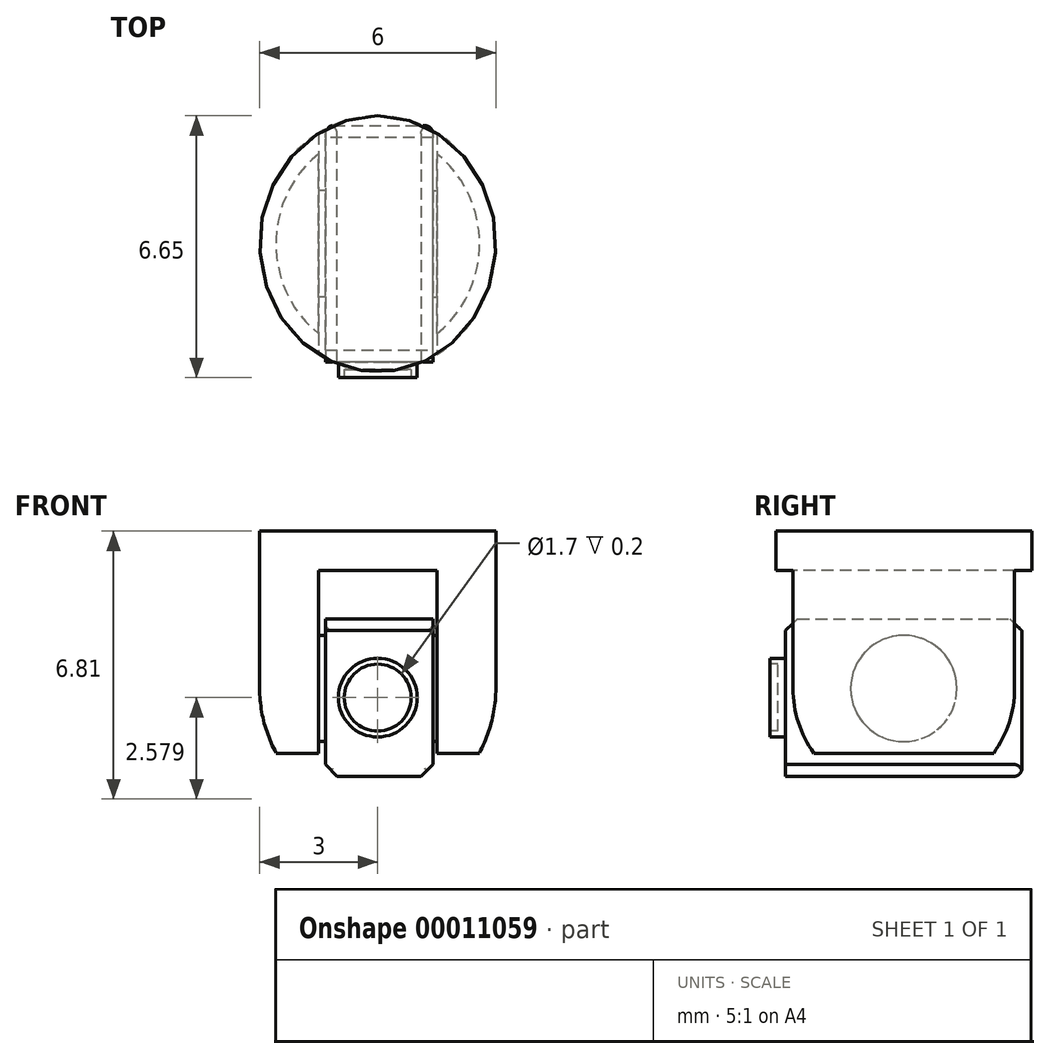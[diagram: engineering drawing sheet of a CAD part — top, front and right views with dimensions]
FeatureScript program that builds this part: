
annotation { "Feature Type Name" : "Feature", "Feature Type Description" : "" }
export const myFeature = defineFeature(function(context is Context, id is Id, definition is map)
    precondition{}
    {
        {
            var Q0;
            Q0=qCreatedBy(makeId("Top.planeOp"),FACE);
            var sketch = newSketch(context, id + "F0", { "sketchPlane" : qUnion([Q0])});
            skEllipse(sketch, "E0", {"center": v(0, 0) * mm, "majorRadius": 3 * mm, "minorRadius": 3.25 * mm, "majorAxis": v(1, 0)});
            skSolve(sketch);
        }
        {
            var Q0;
            Q0 = qSketchRegion(id + "F0", true);
            extrude(context, id + "F1", {"entities" : qUnion([Q0]), "oppositeDirection" : true, "depth" : 4 * mm});
        }
        {
            var Q0;
            Q0=makeQuery(id+"F1.opExtrude","CAP_FACE",FACE,{"disambiguationData":[OSD([sQuery(id+"F0.wireOp",EDGE,"E0")])],"isStart":false});
            var sketch = newSketch(context, id + "F2", { "sketchPlane" : qUnion([Q0])});
            skEllipse(sketch, "E1", {"center": v(0, 0) * mm, "majorRadius": 3.25 * mm, "minorRadius": 3 * mm, "majorAxis": v(0, -1)});
            skLineSegment(sketch, "E2", {"start": v(-3, 0) * mm, "end": v(3, 0) * mm});
            skSolve(sketch);
        }
        {
            var Q0;
            {var subQ0=sQuery(id+"F2.wireOp",EDGE,"E2");Q0=makeQuery(id+"F2.imprint","IMPRINT",FACE,{"disambiguationData":[TD([[makeQuery(id+"F2.imprint","IMPRINT",EDGE,{"derivedFrom":subQ0}),-1.0]])]});}
            var Q1;
            Q1=sQuery(id+"F2.wireOp",EDGE,"E2");
            revolve(context, id + "F3", {"operationType" : NewBodyOperationType.ADD, "entities" : qUnion([Q0]), "axis" : qUnion([Q1]), "revolveType" : RevolveType.FULL});
        }
        {
            var Q0;
            Q0=qCreatedBy(makeId("Top.planeOp"),FACE);
            var sketch = newSketch(context, id + "F4", { "sketchPlane" : qUnion([Q0])});
            skLineSegment(sketch, "E3.rect.bottom", {"start": v(1.5, 4) * mm, "end": v(-1.5, 4) * mm});
            skLineSegment(sketch, "E3.rect.top", {"start": v(1.5, -4) * mm, "end": v(-1.5, -4) * mm});
            skLineSegment(sketch, "E3.rect.left", {"start": v(1.5, 4) * mm, "end": v(1.5, -4) * mm});
            skLineSegment(sketch, "E3.rect.right", {"start": v(-1.5, 4) * mm, "end": v(-1.5, -4) * mm});
            skPoint(sketch, "E3.rect.middle", {"position": v(0, 0) * mm});
            skSolve(sketch);
        }
        {
            var Q0;
            Q0=makeQuery(id+"F4.imprint","IMPRINT",FACE,{"disambiguationData":[TD([[makeQuery(id+"F4.imprint","IMPRINT",EDGE,{"derivedFrom":sQuery(id+"F4.wireOp",EDGE,"E3.rect.bottom")}),1.0]])]});
            extrude(context, id + "F5", {"entities" : qUnion([Q0]), "operationType" : NewBodyOperationType.REMOVE, "oppositeDirection" : true, "depth" : 25 * mm, "hasSecondDirection" : true, "secondDirectionOppositeDirection" : true, "secondDirectionDepth" : 1 * mm});
        }
        {
            var Q0;
            Q0=qCreatedBy(makeId("Front.planeOp"),FACE);
            var sketch = newSketch(context, id + "F6", { "sketchPlane" : qUnion([Q0])});
            skLineSegment(sketch, "E4.rect.bottom", {"start": v(3.25, -7.37) * mm, "end": v(-3.25, -7.37) * mm});
            skLineSegment(sketch, "E4.rect.top", {"start": v(3.25, -5.64) * mm, "end": v(-3.25, -5.64) * mm});
            skLineSegment(sketch, "E4.rect.left", {"start": v(3.25, -7.37) * mm, "end": v(3.25, -5.64) * mm});
            skLineSegment(sketch, "E4.rect.right", {"start": v(-3.25, -7.37) * mm, "end": v(-3.25, -5.64) * mm});
            skPoint(sketch, "E4.rect.middle", {"position": v(0, -6.5) * mm});
            skSolve(sketch);
        }
        {
            var Q0;
            Q0 = qSketchRegion(id + "F6", true);
            extrude(context, id + "F7", {"entities" : qUnion([Q0]), "operationType" : NewBodyOperationType.REMOVE, "endBound" : BoundingType.SYMMETRIC, "oppositeDirection" : true, "depth" : 25 * mm});
        }
        {
            var Q0;
            Q0=makeQuery(id+"F5.boolean.opBoolean","COPY",FACE,{"derivedFrom":makeQuery(id+"F5.opExtrude","SWEPT_FACE",FACE,{"disambiguationData":[OSD([sQuery(id+"F4.wireOp",EDGE,"E3.rect.left")])]})});
            var sketch = newSketch(context, id + "F8", { "sketchPlane" : qUnion([Q0])});
            skCircle(sketch, "E5", {"center": v(0, -4) * mm, "radius": 1.35 * mm});
            skSolve(sketch);
        }
        {
            var Q0;
            Q0 = qSketchRegion(id + "F8", true);
            extrude(context, id + "F9", {"entities" : qUnion([Q0]), "operationType" : NewBodyOperationType.ADD, "depth" : 0.1 * mm});
        }
        {
            var Q0;
            Q0=makeQuery(id+"F5.boolean.opBoolean","COPY",FACE,{"derivedFrom":makeQuery(id+"F5.opExtrude","SWEPT_FACE",FACE,{"disambiguationData":[OSD([sQuery(id+"F4.wireOp",EDGE,"E3.rect.right")])]})});
            var sketch = newSketch(context, id + "F10", { "sketchPlane" : qUnion([Q0])});
            skCircle(sketch, "E6", {"center": v(0, -4) * mm, "radius": 1.35 * mm});
            skSolve(sketch);
        }
        {
            var Q0;
            Q0 = qSketchRegion(id + "F10", true);
            extrude(context, id + "F11", {"entities" : qUnion([Q0]), "operationType" : NewBodyOperationType.ADD, "depth" : 0.17 * mm});
        }
        {
            var Q0;
            Q0=qCreatedBy(makeId("Front.planeOp"),FACE);
            var sketch = newSketch(context, id + "F12", { "sketchPlane" : qUnion([Q0])});
            skPoint(sketch, "E7", {"position": v(-1.5, -4) * mm});
            skPoint(sketch, "E8", {"position": v(1.5, -4) * mm});
            skLineSegment(sketch, "E9", {"start": v(-1.33, 0.8) * mm, "end": v(-1.33, -8.05) * mm, "construction": true});
            skLineSegment(sketch, "E10", {"start": v(1.4, 0.83) * mm, "end": v(1.4, -8.97) * mm, "construction": true});
            skLineSegment(sketch, "E11.bottom", {"start": v(-1.33, -2.23) * mm, "end": v(1.4, -2.23) * mm});
            skLineSegment(sketch, "E11.top", {"start": v(-1.33, -6.23) * mm, "end": v(1.4, -6.23) * mm});
            skLineSegment(sketch, "E11.left", {"start": v(-1.33, -2.23) * mm, "end": v(-1.33, -6.23) * mm});
            skLineSegment(sketch, "E11.right", {"start": v(1.4, -2.23) * mm, "end": v(1.4, -6.23) * mm});
            skSolve(sketch);
        }
        {
            var Q0;
            Q0 = qSketchRegion(id + "F12", true);
            extrude(context, id + "F13", {"entities" : qUnion([Q0]), "depth" : 3 * mm});
        }
        {
            var Q0;
            Q0=makeQuery(id+"F13.opExtrude","CAP_FACE",FACE,{"disambiguationData":[OSD([sQuery(id+"F12.wireOp",EDGE,"E11.bottom"),sQuery(id+"F12.wireOp",EDGE,"E11.top"),sQuery(id+"F12.wireOp",EDGE,"E11.left"),sQuery(id+"F12.wireOp",EDGE,"E11.right")])],"isStart":true});
            extrude(context, id + "F14", {"entities" : qUnion([Q0]), "operationType" : NewBodyOperationType.ADD, "depth" : 3 * mm});
        }
        {
            var Q0;
            Q0=makeQuery(id+"F13.opExtrude","CAP_FACE",FACE,{"disambiguationData":[OSD([sQuery(id+"F12.wireOp",EDGE,"E11.bottom"),sQuery(id+"F12.wireOp",EDGE,"E11.top"),sQuery(id+"F12.wireOp",EDGE,"E11.left"),sQuery(id+"F12.wireOp",EDGE,"E11.right")])],"isStart":false});
            var sketch = newSketch(context, id + "F15", { "sketchPlane" : qUnion([Q0])});
            skSolve(sketch);
        }
        {
            var Q0;
            Q0=makeQuery(id+"F15.imprint","IMPRINT",FACE,{"disambiguationData":[TD([[makeQuery(id+"F15.imprint","IMPRINT",EDGE,{"derivedFrom":makeQuery(id+"F13.opExtrude","CAP_EDGE",EDGE,{"disambiguationData":[OSD([sQuery(id+"F12.wireOp",EDGE,"E11.bottom")])],"isStart":false})}),-1.0]])]});
            var sketch = newSketch(context, id + "F16", { "sketchPlane" : qUnion([Q0])});
            skCircle(sketch, "E12", {"center": v(0, -4.23) * mm, "radius": 1 * mm});
            skSolve(sketch);
        }
        {
            var Q0;
            Q0 = qSketchRegion(id + "F16", true);
            extrude(context, id + "F17", {"entities" : qUnion([Q0]), "operationType" : NewBodyOperationType.ADD, "depth" : 0.4 * mm});
        }
        {
            var Q0;
            Q0=makeQuery(id+"F17.opExtrude","CAP_FACE",FACE,{"disambiguationData":[OSD([sQuery(id+"F16.wireOp",EDGE,"E12")])],"isStart":false});
            var sketch = newSketch(context, id + "F18", { "sketchPlane" : qUnion([Q0])});
            skCircle(sketch, "E13", {"center": v(0, -4.23) * mm, "radius": 0.85 * mm});
            skSolve(sketch);
        }
        {
            var Q0;
            Q0 = qSketchRegion(id + "F18", true);
            extrude(context, id + "F19", {"entities" : qUnion([Q0]), "operationType" : NewBodyOperationType.REMOVE, "oppositeDirection" : true, "depth" : 0.2 * mm});
        }
        {
            var Q0;
            {var subQ0=sQuery(id+"F12.wireOp",EDGE,"E11.top");var subQ1=sQuery(id+"F12.wireOp",EDGE,"E11.left");Q0=makeQuery(id+"F14.boolean.opBoolean","MERGE",EDGE,{"derivedFrom":[makeQuery(id+"F13.opExtrude","SWEPT_EDGE",EDGE,{"disambiguationData":[OSD([subQ0,subQ1])]}),makeQuery(id+"F14.opExtrude","SWEPT_EDGE",EDGE,{"disambiguationData":[OSD([subQ0,subQ1])]})]});}
            var Q1;
            {var subQ0=sQuery(id+"F12.wireOp",EDGE,"E11.top");var subQ1=sQuery(id+"F12.wireOp",EDGE,"E11.right");Q1=makeQuery(id+"F14.boolean.opBoolean","MERGE",EDGE,{"derivedFrom":[makeQuery(id+"F13.opExtrude","SWEPT_EDGE",EDGE,{"disambiguationData":[OSD([subQ0,subQ1])]}),makeQuery(id+"F14.opExtrude","SWEPT_EDGE",EDGE,{"disambiguationData":[OSD([subQ0,subQ1])]})]});}
            var Q2;
            Q2=makeQuery(id+"F13.opExtrude","CAP_EDGE",EDGE,{"disambiguationData":[OSD([sQuery(id+"F12.wireOp",EDGE,"E11.bottom")])],"isStart":false});
            var Q3;
            Q3=makeQuery(id+"F14.opExtrude","CAP_EDGE",EDGE,{"disambiguationData":[OSD([sQuery(id+"F12.wireOp",EDGE,"E11.bottom")])],"isStart":false});
            chamfer(context, id + "F20", {"entities" : qUnion([Q0, Q1, Q2, Q3]), "width" : 0.3 * mm, "tangentPropagation" : true});
        }
        {
            var Q0;
            Q0=makeQuery(id+"F14.opExtrude","CAP_EDGE",EDGE,{"disambiguationData":[OSD([sQuery(id+"F12.wireOp",EDGE,"E11.right")])],"isStart":false});
            var Q1;
            Q1=makeQuery(id+"F14.opExtrude","CAP_EDGE",EDGE,{"disambiguationData":[OSD([sQuery(id+"F12.wireOp",EDGE,"E11.left")])],"isStart":false});
            var Q2;
            Q2=makeQuery(id+"F14.opExtrude","CAP_EDGE",EDGE,{"disambiguationData":[OSD([sQuery(id+"F12.wireOp",EDGE,"E11.top")])],"isStart":false});
            fillet(context, id + "F21", {"entities" : qUnion([Q0, Q1, Q2]), "radius" : 0.2 * mm, "tangentPropagation" : true, "allowEdgeOverflow" : false});
        }
    });
